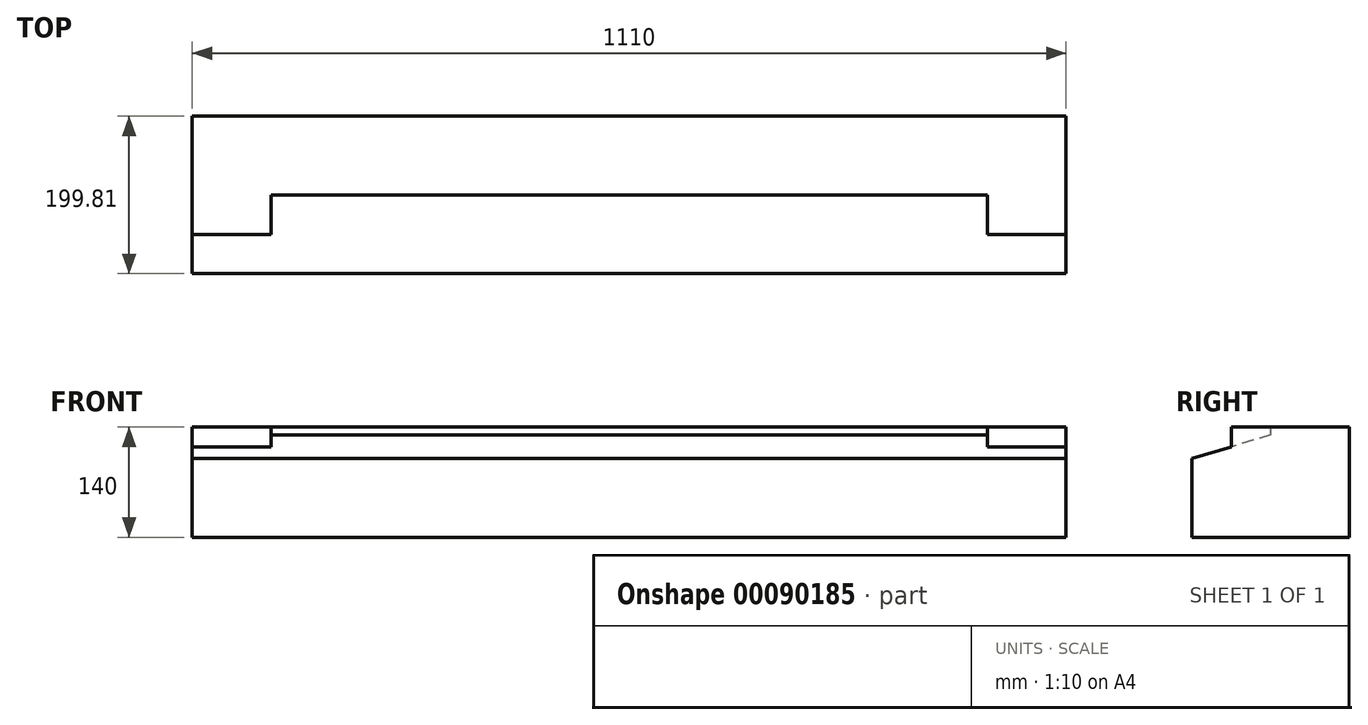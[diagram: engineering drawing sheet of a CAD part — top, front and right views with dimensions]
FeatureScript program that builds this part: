
annotation { "Feature Type Name" : "Feature", "Feature Type Description" : "" }
export const myFeature = defineFeature(function(context is Context, id is Id, definition is map)
    precondition{}
    {
        {
            var Q0;
            Q0=qCreatedBy(makeId("Right.planeOp"),FACE);
            var sketch = newSketch(context, id + "F0", { "sketchPlane" : qUnion([Q0])});
            skLineSegment(sketch, "E0.bottom", {"start": v(0, 31.43) * mm, "end": v(100, 31.43) * mm});
            skLineSegment(sketch, "E0.top", {"start": v(-99.81, -108.57) * mm, "end": v(100, -108.57) * mm});
            skLineSegment(sketch, "E0.left", {"start": v(-99.81, -8.57) * mm, "end": v(-99.81, -108.57) * mm});
            skLineSegment(sketch, "E0.right", {"start": v(100, 31.43) * mm, "end": v(100, -108.57) * mm});
            skLineSegment(sketch, "E1", {"start": v(0, 31.43) * mm, "end": v(0, 21.43) * mm});
            skLineSegment(sketch, "E2", {"start": v(0, 21.43) * mm, "end": v(-99.81, -8.57) * mm});
            skPoint(sketch, "E3", {"position": v(0, 0) * mm});
            skSolve(sketch);
        }
        {
            var Q0;
            Q0=makeQuery(id+"F0.imprint","IMPRINT",FACE,{"disambiguationData":[TD([[makeQuery(id+"F0.imprint","IMPRINT",EDGE,{"derivedFrom":sQuery(id+"F0.wireOp",EDGE,"E0.bottom")}),-1.0]])]});
            extrude(context, id + "F1", {"entities" : qUnion([Q0]), "depth" : (910 / 2) * mm});
        }
        {
            var Q0;
            Q0=makeQuery(id+"F1.opExtrude","CAP_FACE",FACE,{"disambiguationData":[OSD([sQuery(id+"F0.wireOp",EDGE,"E0.bottom"),sQuery(id+"F0.wireOp",EDGE,"E0.top"),sQuery(id+"F0.wireOp",EDGE,"E0.left"),sQuery(id+"F0.wireOp",EDGE,"E0.right"),sQuery(id+"F0.wireOp",EDGE,"E1"),sQuery(id+"F0.wireOp",EDGE,"E2")])],"isStart":false});
            var sketch = newSketch(context, id + "F2", { "sketchPlane" : qUnion([Q0])});
            skLineSegment(sketch, "E4", {"start": v(100, -108.57) * mm, "end": v(-99.81, -108.57) * mm});
            skLineSegment(sketch, "E5", {"start": v(-99.81, -108.57) * mm, "end": v(-99.81, -8.57) * mm});
            skLineSegment(sketch, "E6", {"start": v(-99.81, -8.57) * mm, "end": v(-50, 6.4) * mm});
            skLineSegment(sketch, "E7", {"start": v(-50, 6.4) * mm, "end": v(-50, 31.43) * mm});
            skLineSegment(sketch, "E8", {"start": v(-50, 31.43) * mm, "end": v(100, 31.43) * mm});
            skLineSegment(sketch, "E9", {"start": v(100, 31.43) * mm, "end": v(100, -108.57) * mm});
            skSolve(sketch);
        }
        {
            var Q0;
            Q0=makeQuery(id+"F2.imprint","IMPRINT",FACE,{"disambiguationData":[TD([[makeQuery(id+"F2.imprint","IMPRINT",EDGE,{"derivedFrom":sQuery(id+"F2.wireOp",EDGE,"E4")}),1.0]])]});
            var Q1;
            {var subQ0=sQuery(id+"F2.wireOp",EDGE,"E7");Q1=makeQuery(id+"F2.imprint","IMPRINT",FACE,{"disambiguationData":[TD([[makeQuery(id+"F2.imprint","IMPRINT",EDGE,{"derivedFrom":subQ0}),-1.0]])]});}
            extrude(context, id + "F3", {"entities" : qUnion([Q0, Q1]), "operationType" : NewBodyOperationType.ADD, "depth" : 100 * mm});
        }
        {
            var Q0;
            Q0=makeQuery(id+"F1.opExtrude","SWEPT_BODY",BODY,{"disambiguationData":[OSD([sQuery(id+"F0.wireOp",EDGE,"E0.bottom"),sQuery(id+"F0.wireOp",EDGE,"E0.top"),sQuery(id+"F0.wireOp",EDGE,"E0.left"),sQuery(id+"F0.wireOp",EDGE,"E0.right"),sQuery(id+"F0.wireOp",EDGE,"E1"),sQuery(id+"F0.wireOp",EDGE,"E2")])]});
            var Q1;
            Q1=makeQuery(id+"F1.opExtrude","CAP_FACE",FACE,{"disambiguationData":[OSD([sQuery(id+"F0.wireOp",EDGE,"E0.bottom"),sQuery(id+"F0.wireOp",EDGE,"E0.top"),sQuery(id+"F0.wireOp",EDGE,"E0.left"),sQuery(id+"F0.wireOp",EDGE,"E0.right"),sQuery(id+"F0.wireOp",EDGE,"E1"),sQuery(id+"F0.wireOp",EDGE,"E2")])],"isStart":true});
            mirror(context, id + "F4", {"operationType" : NewBodyOperationType.ADD, "entities" : qUnion([Q0]), "mirrorPlane" : qUnion([Q1])});
        }
    });
